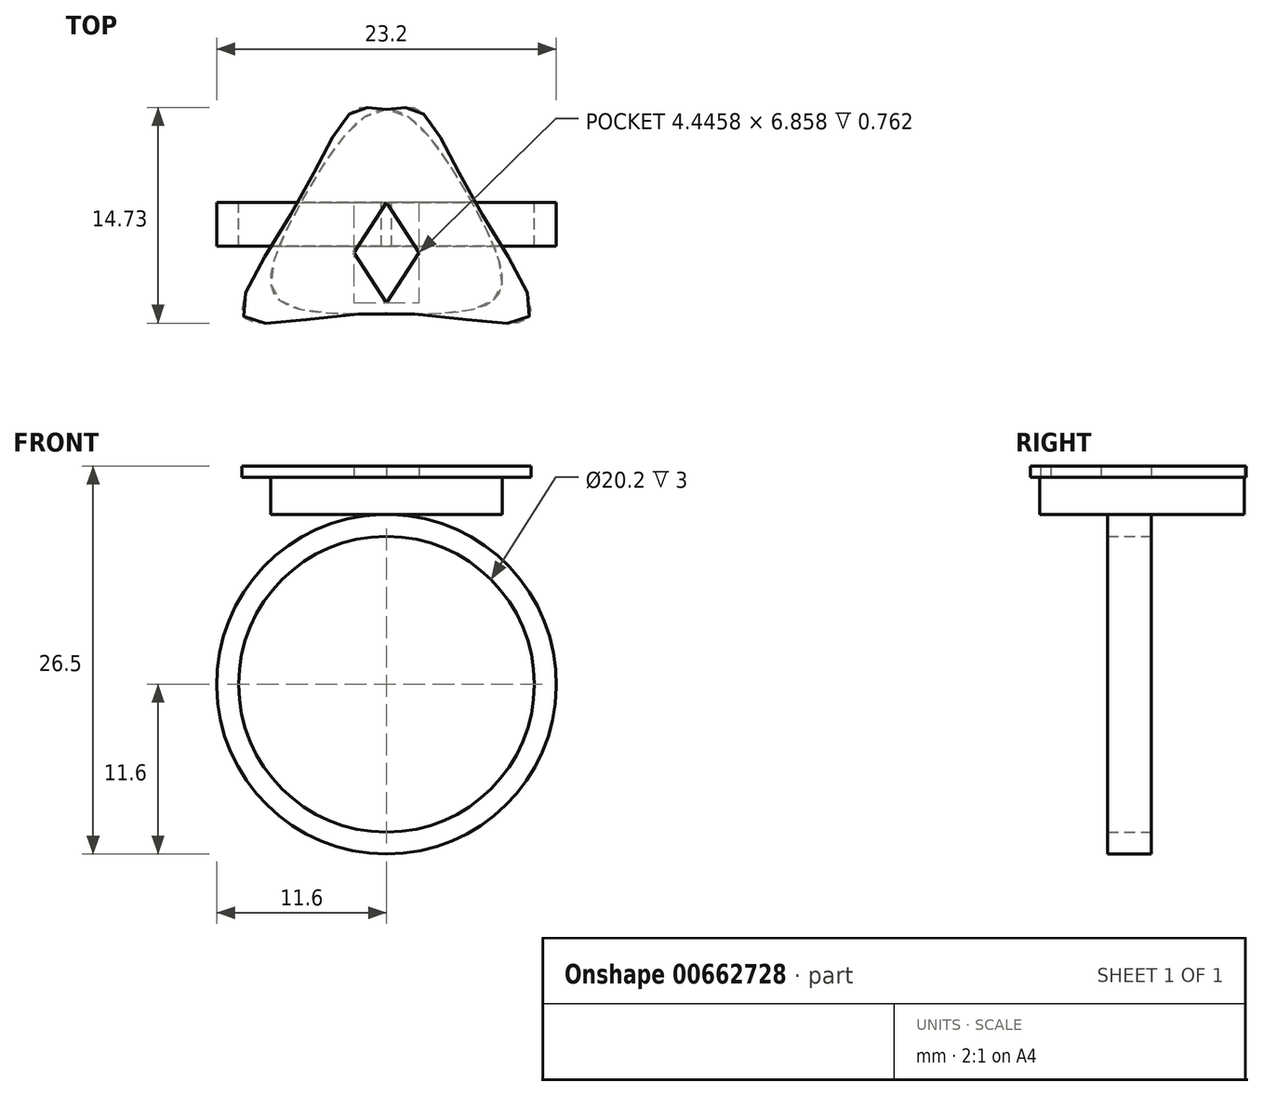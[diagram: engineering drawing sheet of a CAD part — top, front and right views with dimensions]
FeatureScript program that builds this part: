
annotation { "Feature Type Name" : "Feature", "Feature Type Description" : "" }
export const myFeature = defineFeature(function(context is Context, id is Id, definition is map)
    precondition{}
    {
        {
            var Q0;
            Q0=qCreatedBy(makeId("Front.planeOp"),FACE);
            var sketch = newSketch(context, id + "F0", { "sketchPlane" : qUnion([Q0])});
            skCircle(sketch, "E0", {"center": v(0, 0) * mm, "radius": 10.1 * mm});
            skCircle(sketch, "E1", {"center": v(0, 0) * mm, "radius": 11.6 * mm});
            skSolve(sketch);
        }
        {
            var Q0;
            Q0 = qSketchRegion(id + "F0", true);
            extrude(context, id + "F1", {"entities" : qUnion([Q0]), "depth" : 3 * mm, "offsetDistance" : 25.4 * mm});
        }
        {
            var Q0;
            Q0=qCreatedBy(makeId("Top.planeOp"),FACE);
            cPlane(context, id + "F2", {"entities" : qUnion([Q0]), "cplaneType" : CPlaneType.OFFSET, "offset" : 11.6 * mm, "width" : 152.4 * mm, "height" : 152.4 * mm});
        }
        {
            var Q0;
            Q0=qCreatedBy(id+"F2.planeOp",FACE);
            var sketch = newSketch(context, id + "F3", { "sketchPlane" : qUnion([Q0])});
            skFitSpline(sketch, "E2", {"points": [v(0, 6.35) * mm, v(-5.84, 0) * mm, v(-7.62, -6.35) * mm, v(0, -7.62) * mm, v(7.62, -6.35) * mm, v(5.84, 0) * mm, v(0, 6.35) * mm]});
            skSolve(sketch);
        }
        {
            var Q0;
            Q0 = qSketchRegion(id + "F3", true);
            extrude(context, id + "F4", {"entities" : qUnion([Q0]), "operationType" : NewBodyOperationType.ADD, "depth" : 2.54 * mm, "offsetDistance" : 25.4 * mm});
        }
        {
            var Q0;
            Q0=makeQuery(id+"F4.opExtrude","CAP_FACE",FACE,{"disambiguationData":[OSD([sQuery(id+"F3.wireOp",EDGE,"E2")])],"isStart":false});
            var sketch = newSketch(context, id + "F5", { "sketchPlane" : qUnion([Q0])});
            skFitSpline(sketch, "E3.0.0", {"points": [v(0, 6.35) * mm, v(-2.08, 6.35) * mm, v(-5.97, 0.15) * mm, v(-9.76, -7.76) * mm, v(0, -7.55) * mm, v(9.76, -7.76) * mm, v(5.97, 0.15) * mm, v(2.08, 6.35) * mm, v(0, 6.35) * mm]});
            skFitSpline(sketch, "E4.0", {"points": [v(0.17, 5.58) * mm, v(0, 5.6) * mm, v(-0.17, 5.58) * mm, v(-0.41, 5.53) * mm, v(-0.74, 5.4) * mm, v(-1.19, 5.13) * mm, v(-1.82, 4.6) * mm, v(-2.64, 3.68) * mm, v(-3.63, 2.28) * mm, v(-4.42, 0.97) * mm, v(-5.02, -0.1) * mm, v(-5.61, -1.16) * mm, v(-6.27, -2.42) * mm, v(-6.77, -3.57) * mm, v(-7.03, -4.37) * mm, v(-7.14, -4.9) * mm, v(-7.17, -5.33) * mm, v(-7.13, -5.65) * mm, v(-7.05, -5.84) * mm, v(-6.97, -5.95) * mm, v(-6.85, -6.08) * mm, v(-6.64, -6.23) * mm, v(-6.24, -6.41) * mm, v(-5.71, -6.56) * mm, v(-4.87, -6.72) * mm, v(-3.6, -6.83) * mm, v(-2.15, -6.86) * mm, v(-0.93, -6.86) * mm, v(0, -6.86) * mm, v(0.93, -6.86) * mm, v(2.15, -6.86) * mm, v(3.6, -6.83) * mm, v(4.87, -6.72) * mm, v(5.71, -6.56) * mm, v(6.24, -6.41) * mm, v(6.64, -6.23) * mm, v(6.85, -6.08) * mm, v(6.97, -5.95) * mm, v(7.05, -5.84) * mm, v(7.13, -5.65) * mm, v(7.17, -5.33) * mm, v(7.14, -4.9) * mm, v(7.03, -4.37) * mm, v(6.77, -3.57) * mm, v(6.27, -2.42) * mm, v(5.61, -1.16) * mm, v(5.02, -0.1) * mm, v(4.42, 0.97) * mm, v(3.63, 2.28) * mm, v(2.64, 3.68) * mm, v(1.82, 4.6) * mm, v(1.19, 5.13) * mm, v(0.74, 5.4) * mm, v(0.41, 5.53) * mm, v(0.17, 5.58) * mm, v(0, 5.6) * mm, v(-0.17, 5.58) * mm, v(0.17, 5.58) * mm]});
            skLineSegment(sketch, "E5", {"start": v(-2.48, 3.83) * mm, "end": v(-0.3, 0.47) * mm});
            skLineSegment(sketch, "E6", {"start": v(-2.53, -2.96) * mm, "end": v(-4.73, 0.43) * mm});
            skLineSegment(sketch, "E7", {"start": v(-2.22, -3.43) * mm, "end": v(0, -6.86) * mm});
            skLineSegment(sketch, "E8", {"start": v(0, 0) * mm, "end": v(-2.22, -3.43) * mm});
            skLineSegment(sketch, "E9", {"start": v(0, 7.93) * mm, "end": v(0, 10.92) * mm, "construction": true});
            skLineSegment(sketch, "E10.MirrorCS", {"start": v(2.48, 3.83) * mm, "end": v(0.3, 0.47) * mm});
            skLineSegment(sketch, "E11.MirrorCS", {"start": v(0, 0) * mm, "end": v(2.22, -3.43) * mm});
            skLineSegment(sketch, "E12.MirrorCS", {"start": v(2.53, -2.96) * mm, "end": v(4.73, 0.43) * mm});
            skLineSegment(sketch, "E13.MirrorCS", {"start": v(2.22, -3.43) * mm, "end": v(0, -6.86) * mm});
            skLineSegment(sketch, "E14", {"start": v(2.14, 4.23) * mm, "end": v(0, 0.93) * mm});
            skLineSegment(sketch, "E15", {"start": v(-5, -0.07) * mm, "end": v(-2.83, -3.43) * mm});
            skLineSegment(sketch, "E16.MirrorCS", {"start": v(-2.14, 4.23) * mm, "end": v(0, 0.93) * mm});
            skLineSegment(sketch, "E17.MirrorCS", {"start": v(5, -0.07) * mm, "end": v(2.83, -3.43) * mm});
            skLineSegment(sketch, "E18.trimOffspring", {"start": v(0.3, 0.47) * mm, "end": v(2.53, -2.96) * mm});
            skLineSegment(sketch, "E19.trimOffspring", {"start": v(-0.3, 0.47) * mm, "end": v(-2.53, -2.96) * mm});
            skPoint(sketch, "E20.orphan", {"position": v(0, 0) * mm});
            skLineSegment(sketch, "E21.trimOffspring", {"start": v(2.83, -3.43) * mm, "end": v(4.94, -6.7) * mm});
            skPoint(sketch, "E22.orphan", {"position": v(2.22, -3.43) * mm});
            skLineSegment(sketch, "E23.trimOffspring", {"start": v(2.53, -3.9) * mm, "end": v(4.38, -6.76) * mm});
            skLineSegment(sketch, "E24.trimOffspring", {"start": v(2.53, -3.9) * mm, "end": v(0.6, -6.86) * mm});
            skLineSegment(sketch, "E25.trimOffspring", {"start": v(-2.83, -3.43) * mm, "end": v(-4.94, -6.7) * mm});
            skLineSegment(sketch, "E26.trimOffspring", {"start": v(-2.53, -3.9) * mm, "end": v(-0.6, -6.86) * mm});
            skLineSegment(sketch, "E27.trimOffspring", {"start": v(-2.53, -3.9) * mm, "end": v(-4.38, -6.76) * mm});
            skSolve(sketch);
        }
        {
            var Q0;
            Q0 = qSketchRegion(id + "F5", true);
            var Q1;
            {var subQ11=sQuery(id+"F5.wireOp",EDGE,"E5");Q1=makeQuery(id+"F5.imprint","IMPRINT",FACE,{"disambiguationData":[TD([[makeQuery(id+"F5.imprint","IMPRINT",EDGE,{"derivedFrom":subQ11}),1.0]])]});}
            extrude(context, id + "F6", {"entities" : qUnion([Q0, Q1]), "operationType" : NewBodyOperationType.ADD, "depth" : 0.76 * mm, "offsetDistance" : 25.4 * mm});
        }
    });
